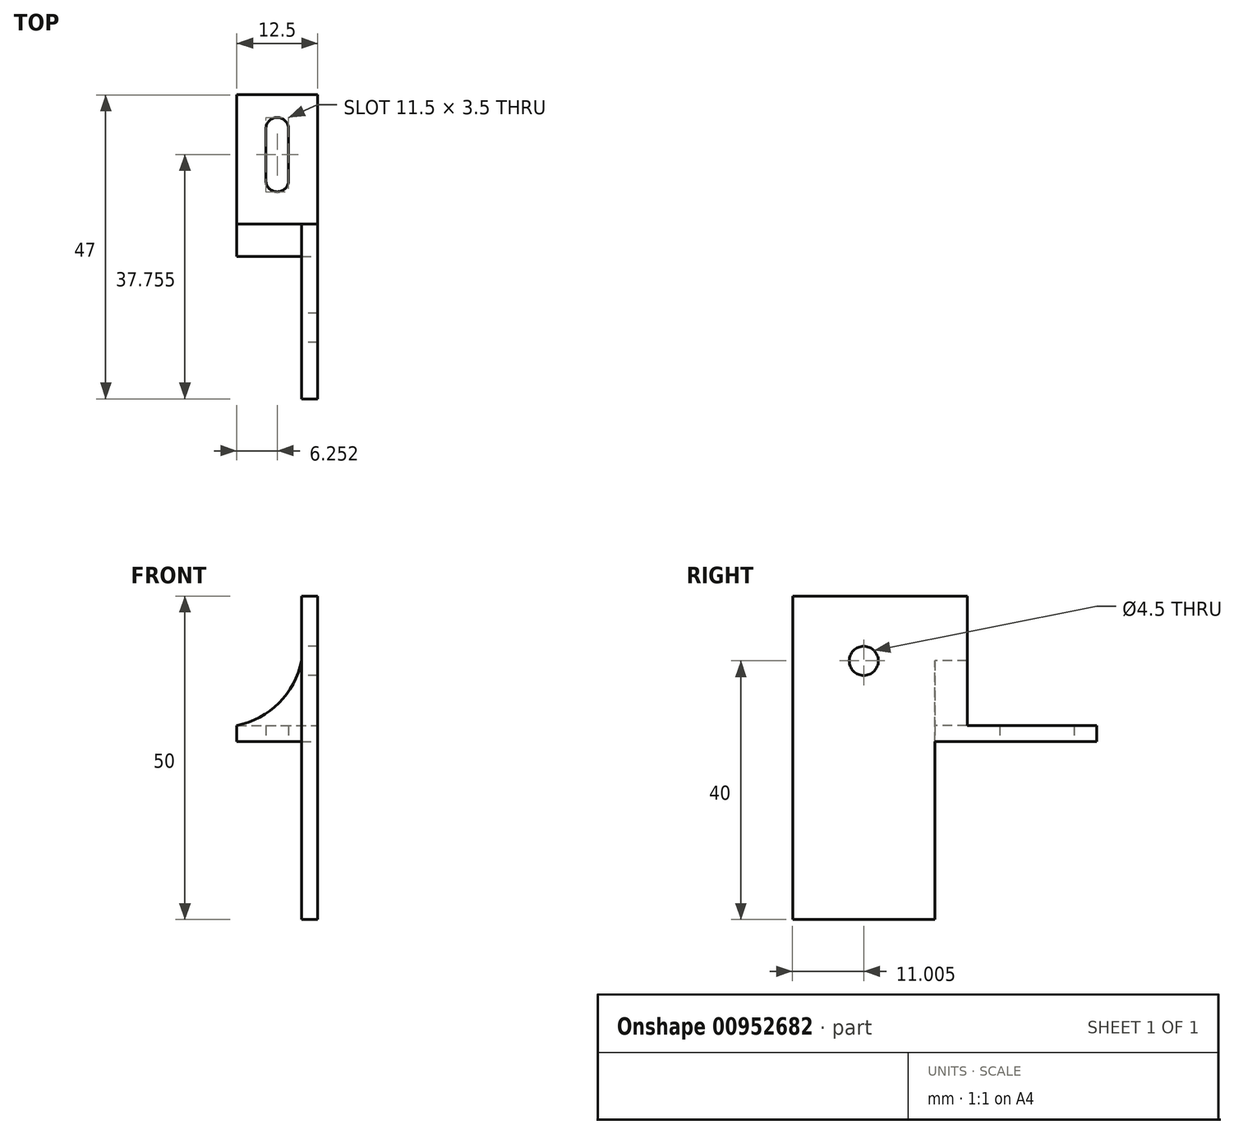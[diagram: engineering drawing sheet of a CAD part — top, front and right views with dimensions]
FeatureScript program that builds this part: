
annotation { "Feature Type Name" : "Feature", "Feature Type Description" : "" }
export const myFeature = defineFeature(function(context is Context, id is Id, definition is map)
    precondition{}
    {
        {
            var Q0;
            Q0=qCreatedBy(makeId("Top.planeOp"),FACE);
            var sketch = newSketch(context, id + "F0", { "sketchPlane" : qUnion([Q0])});
            skLineSegment(sketch, "E0.bottom", {"start": v(-9.7, 25.08) * mm, "end": v(2.8, 25.08) * mm});
            skLineSegment(sketch, "E0.top", {"start": v(-9.7, 0.08) * mm, "end": v(2.8, 0.08) * mm});
            skLineSegment(sketch, "E0.left", {"start": v(-9.7, 25.08) * mm, "end": v(-9.7, 0.08) * mm});
            skLineSegment(sketch, "E0.right", {"start": v(2.8, 25.08) * mm, "end": v(2.8, 0.08) * mm});
            skLineSegment(sketch, "E1", {"start": v(-3.45, 25.08) * mm, "end": v(-3.45, 0.08) * mm, "construction": true});
            skPoint(sketch, "E2", {"position": v(-5.2, 19.83) * mm});
            skPoint(sketch, "E3", {"position": v(-5.2, 11.83) * mm});
            skPoint(sketch, "E4", {"position": v(-1.7, 11.83) * mm});
            skPoint(sketch, "E5", {"position": v(-1.7, 19.83) * mm});
            skLineSegment(sketch, "E6", {"start": v(-5.2, 11.83) * mm, "end": v(-5.2, 11.83) * mm});
            skLineSegment(sketch, "E7", {"start": v(-1.7, 11.83) * mm, "end": v(-1.7, 19.83) * mm});
            skArc(sketch, "E8", {"start": v(-1.7, 19.83) * mm, "mid": v(-3.45, 21.58) * mm, "end": v(-5.2, 19.83) * mm});
            skArc(sketch, "E9", {"start": v(-5.2, 19.83) * mm, "mid": v(-3.45, 18.08) * mm, "end": v(-1.7, 19.83) * mm, "construction": true});
            skLineSegment(sketch, "E10", {"start": v(-5.2, 11.83) * mm, "end": v(-5.2, 19.83) * mm});
            skArc(sketch, "E11", {"start": v(-5.2, 11.83) * mm, "mid": v(-3.45, 10.08) * mm, "end": v(-1.7, 11.83) * mm});
            skArc(sketch, "E12", {"start": v(-1.7, 11.83) * mm, "mid": v(-3.45, 13.58) * mm, "end": v(-5.2, 11.83) * mm, "construction": true});
            skPoint(sketch, "E13", {"position": v(-3.45, 21.58) * mm});
            skPoint(sketch, "E14", {"position": v(-3.45, 10.08) * mm});
            skSolve(sketch);
        }
        {
            var Q0;
            Q0=makeQuery(id+"F0.imprint","IMPRINT",FACE,{"disambiguationData":[TD([[makeQuery(id+"F0.imprint","IMPRINT",EDGE,{"derivedFrom":sQuery(id+"F0.wireOp",EDGE,"E0.bottom")}),-1.0]])]});
            extrude(context, id + "F1", {"entities" : qUnion([Q0]), "depth" : 2.5 * mm, "offsetDistance" : 25 * mm});
        }
        {
            var Q0;
            Q0=makeQuery(id+"F1.opExtrude","SWEPT_FACE",FACE,{"disambiguationData":[OSD([sQuery(id+"F0.wireOp",EDGE,"E0.top")])]});
            var sketch = newSketch(context, id + "F2", { "sketchPlane" : qUnion([Q0])});
            skLineSegment(sketch, "E15.bottom", {"start": v(2.8, -27.5) * mm, "end": v(0.3, -27.5) * mm});
            skLineSegment(sketch, "E15.top", {"start": v(2.8, 22.5) * mm, "end": v(0.3, 22.5) * mm});
            skLineSegment(sketch, "E15.left", {"start": v(2.8, -27.5) * mm, "end": v(2.8, 22.5) * mm});
            skLineSegment(sketch, "E15.right", {"start": v(0.3, -27.5) * mm, "end": v(0.3, 22.5) * mm});
            skPoint(sketch, "E16", {"position": v(2.8, 2.5) * mm});
            skSolve(sketch);
        }
        {
            var Q0;
            {var subQ0=sQuery(id+"F2.wireOp",EDGE,"E15.top");Q0=makeQuery(id+"F2.imprint","IMPRINT",FACE,{"disambiguationData":[TD([[makeQuery(id+"F2.imprint","IMPRINT",EDGE,{"derivedFrom":subQ0}),1.0]])]});}
            var Q1;
            {var subQ0=sQuery(id+"F2.wireOp",EDGE,"E15.left");var subQ1=sQuery(id+"F0.wireOp",EDGE,"E0.top");var subQ2=makeQuery(id+"F1.opExtrude","CAP_EDGE",EDGE,{"disambiguationData":[OSD([subQ1])],"isStart":true});var subQ3=makeQuery(id+"F2.imprint","INTERSECT",VERTEX,{"derivedFrom":[subQ2,subQ0]});var subQ4=makeQuery(id+"F1.opExtrude","CAP_EDGE",EDGE,{"disambiguationData":[OSD([subQ1])],"isStart":false});var subQ5=makeQuery(id+"F2.imprint","INTERSECT",VERTEX,{"derivedFrom":[subQ4,subQ0]});Q1=makeQuery(id+"F2.imprint","IMPRINT",FACE,{"disambiguationData":[TD([[makeQuery(id+"F2.imprint","IMPRINT",EDGE,{"disambiguationData":[TD([[subQ3,1.0],[subQ5,-1.0]])],"derivedFrom":subQ0}),-1.0]])]});}
            var Q2;
            {var subQ0=sQuery(id+"F2.wireOp",EDGE,"E15.bottom");Q2=makeQuery(id+"F2.imprint","IMPRINT",FACE,{"disambiguationData":[TD([[makeQuery(id+"F2.imprint","IMPRINT",EDGE,{"derivedFrom":subQ0}),-1.0]])]});}
            extrude(context, id + "F3", {"entities" : qUnion([Q0, Q1, Q2]), "operationType" : NewBodyOperationType.ADD, "depth" : 22 * mm, "offsetDistance" : 25 * mm});
        }
        {
            var Q0;
            {var subQ0=sQuery(id+"F2.wireOp",EDGE,"E15.top");var subQ2=sQuery(id+"F2.wireOp",EDGE,"E15.left");var subQ4=sQuery(id+"F2.wireOp",EDGE,"E15.right");Q0=makeQuery(id+"F3.boolean.opBoolean","SPLIT",FACE,{"disambiguationData":[TD([makeQuery(id+"F3.opExtrude","SWEPT_FACE",FACE,{"disambiguationData":[OSD([subQ0])]})])],"derivedFrom":makeQuery(id+"F3.opExtrude","CAP_FACE",FACE,{"disambiguationData":[OSD([sQuery(id+"F2.wireOp",EDGE,"E15.bottom"),subQ0,subQ2,subQ4])],"isStart":true})});}
            extrude(context, id + "F4", {"entities" : qUnion([Q0]), "operationType" : NewBodyOperationType.ADD, "depth" : 5 * mm, "offsetDistance" : 25 * mm});
        }
        {
            var Q0;
            {var subQ0=sQuery(id+"F2.wireOp",EDGE,"E15.right");Q0=makeQuery(id+"F4.boolean.opBoolean","MERGE",FACE,{"derivedFrom":[makeQuery(id+"F3.opExtrude","SWEPT_FACE",FACE,{"disambiguationData":[OSD([subQ0])]}),makeQuery(id+"F4.opExtrude","SWEPT_FACE",FACE,{"disambiguationData":[OSD([subQ0])]})]});}
            var sketch = newSketch(context, id + "F5", { "sketchPlane" : qUnion([Q0])});
            skLineSegment(sketch, "E17", {"start": v(10.92, -27.5) * mm, "end": v(10.92, 22.5) * mm, "construction": true});
            skCircle(sketch, "E18", {"center": v(10.92, 12.5) * mm, "radius": 2.25 * mm});
            skSolve(sketch);
        }
        {
            var Q0;
            Q0=makeQuery(id+"F5.imprint","IMPRINT",FACE,{"disambiguationData":[TD([[makeQuery(id+"F5.imprint","IMPRINT",EDGE,{"derivedFrom":sQuery(id+"F5.wireOp",EDGE,"E18")}),1.0]])]});
            extrude(context, id + "F6", {"entities" : qUnion([Q0]), "operationType" : NewBodyOperationType.REMOVE, "oppositeDirection" : true, "depth" : 25 * mm, "offsetDistance" : 25 * mm});
        }
        {
            var Q0;
            Q0=makeQuery(id+"F1.opExtrude","SWEPT_FACE",FACE,{"disambiguationData":[OSD([sQuery(id+"F0.wireOp",EDGE,"E0.top")])]});
            cPlane(context, id + "F7", {"entities" : qUnion([Q0]), "cplaneType" : CPlaneType.OFFSET, "offset" : 0 * mm, "width" : 150 * mm, "height" : 150 * mm});
        }
        {
            var Q0;
            Q0=qCreatedBy(id+"F7.planeOp",FACE);
            var sketch = newSketch(context, id + "F8", { "sketchPlane" : qUnion([Q0])});
            skLineSegment(sketch, "E19.0.0", {"start": v(-9.7, 0) * mm, "end": v(0.3, 0) * mm});
            skLineSegment(sketch, "E19.0.1", {"start": v(0.3, 0) * mm, "end": v(0.3, 2.5) * mm});
            skLineSegment(sketch, "E19.0.2", {"start": v(0.3, 2.5) * mm, "end": v(-9.7, 2.5) * mm});
            skLineSegment(sketch, "E19.0.3", {"start": v(-9.7, 2.5) * mm, "end": v(-9.7, 0) * mm});
            skLineSegment(sketch, "E20.0.0", {"start": v(0.3, 0) * mm, "end": v(0.3, -27.5) * mm});
            skLineSegment(sketch, "E20.0.2", {"start": v(0.3, -27.5) * mm, "end": v(0.3, 22.5) * mm});
            skLineSegment(sketch, "E20.0.4", {"start": v(0.3, 22.5) * mm, "end": v(0.3, 2.5) * mm});
            skLineSegment(sketch, "E20.0.6", {"start": v(0.3, 2.5) * mm, "end": v(0.3, 0) * mm});
            skLineSegment(sketch, "E21", {"start": v(-9.7, 2.5) * mm, "end": v(0.3, 12.5) * mm});
            skSolve(sketch);
        }
        {
            var Q0;
            {var subQ0=sQuery(id+"F8.wireOp",EDGE,"E19.0.2");Q0=makeQuery(id+"F8.imprint","IMPRINT",FACE,{"disambiguationData":[TD([[makeQuery(id+"F8.imprint","IMPRINT",EDGE,{"derivedFrom":subQ0}),-1.0]])]});}
            extrude(context, id + "F9", {"entities" : qUnion([Q0]), "operationType" : NewBodyOperationType.ADD, "oppositeDirection" : true, "depth" : 5 * mm, "offsetDistance" : 25 * mm});
        }
        {
            var Q0;
            Q0=makeQuery(id+"F9.boolean.opBoolean","MERGE",FACE,{"derivedFrom":[makeQuery(id+"F4.opExtrude","CAP_FACE",FACE,{"disambiguationData":[OSD([sQuery(id+"F2.wireOp",EDGE,"E15.bottom"),sQuery(id+"F2.wireOp",EDGE,"E15.top"),sQuery(id+"F2.wireOp",EDGE,"E15.left"),sQuery(id+"F2.wireOp",EDGE,"E15.right")])],"isStart":false}),makeQuery(id+"F9.opExtrude","CAP_FACE",FACE,{"disambiguationData":[OSD([sQuery(id+"F8.wireOp",EDGE,"E19.0.2"),sQuery(id+"F8.wireOp",EDGE,"E20.0.4"),sQuery(id+"F8.wireOp",EDGE,"E21")])],"isStart":false})]});
            var sketch = newSketch(context, id + "F10", { "sketchPlane" : qUnion([Q0])});
            skArc(sketch, "E22", {"start": v(-0.3, 12.5) * mm, "mid": v(3.19, 6) * mm, "end": v(9.7, 2.5) * mm});
            skSolve(sketch);
        }
        {
            var Q0;
            Q0=makeQuery(id+"F10.imprint","IMPRINT",FACE,{"disambiguationData":[TD([[makeQuery(id+"F10.imprint","IMPRINT",EDGE,{"derivedFrom":sQuery(id+"F10.wireOp",EDGE,"E22")}),1.0]])]});
            extrude(context, id + "F11", {"entities" : qUnion([Q0]), "operationType" : NewBodyOperationType.REMOVE, "oppositeDirection" : true, "depth" : 25 * mm, "offsetDistance" : 25 * mm});
        }
    });
